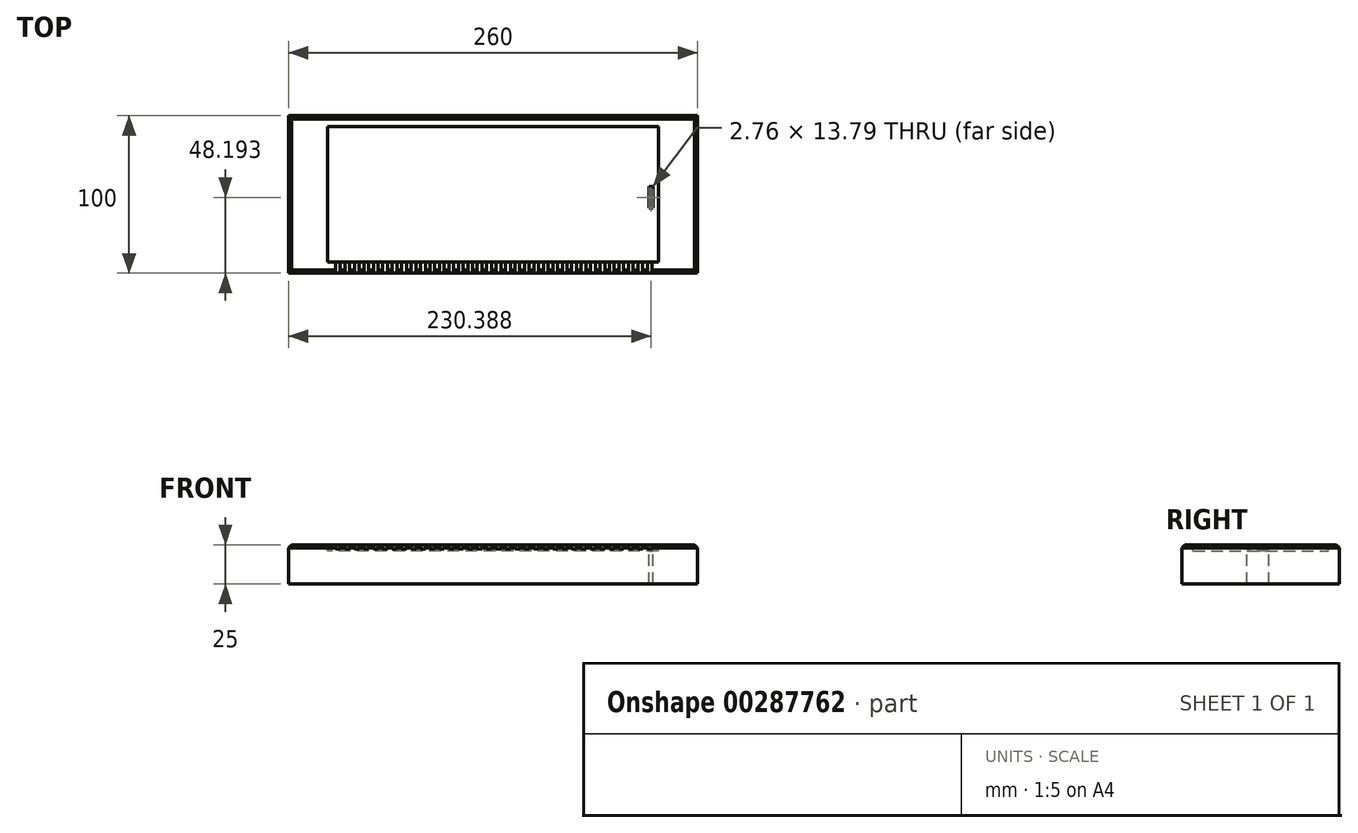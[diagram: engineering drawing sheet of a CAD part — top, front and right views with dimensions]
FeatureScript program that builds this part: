
annotation { "Feature Type Name" : "Feature", "Feature Type Description" : "" }
export const myFeature = defineFeature(function(context is Context, id is Id, definition is map)
    precondition{}
    {
        {
            var Q0;
            Q0=qCreatedBy(makeId("Top.planeOp"),FACE);
            var sketch = newSketch(context, id + "F0", { "sketchPlane" : qUnion([Q0])});
            skLineSegment(sketch, "E0.bottom", {"start": v(130, -50) * mm, "end": v(-130, -50) * mm});
            skLineSegment(sketch, "E0.top", {"start": v(130, 50) * mm, "end": v(-130, 50) * mm});
            skLineSegment(sketch, "E0.left", {"start": v(130, -50) * mm, "end": v(130, 50) * mm});
            skLineSegment(sketch, "E0.right", {"start": v(-130, -50) * mm, "end": v(-130, 50) * mm});
            skPoint(sketch, "E0.middle", {"position": v(0, 0) * mm});
            skSolve(sketch);
        }
        {
            var Q0;
            Q0 = qSketchRegion(id + "F0", true);
            extrude(context, id + "F1", {"entities" : qUnion([Q0]), "depth" : 25 * mm});
        }
        {
            var Q0;
            Q0=makeQuery(id+"F1.opExtrude","CAP_FACE",FACE,{"disambiguationData":[OSD([sQuery(id+"F0.wireOp",EDGE,"E0.bottom"),sQuery(id+"F0.wireOp",EDGE,"E0.top"),sQuery(id+"F0.wireOp",EDGE,"E0.left"),sQuery(id+"F0.wireOp",EDGE,"E0.right")])],"isStart":false});
            var sketch = newSketch(context, id + "F2", { "sketchPlane" : qUnion([Q0])});
            skLineSegment(sketch, "E1.bottom", {"start": v(105, -43) * mm, "end": v(-105, -43) * mm});
            skLineSegment(sketch, "E1.top", {"start": v(105, 43) * mm, "end": v(-105, 43) * mm});
            skLineSegment(sketch, "E1.left", {"start": v(105, -43) * mm, "end": v(105, 43) * mm});
            skLineSegment(sketch, "E1.right", {"start": v(-105, -43) * mm, "end": v(-105, 43) * mm});
            skPoint(sketch, "E1.middle", {"position": v(0, 0) * mm});
            skSolve(sketch);
        }
        {
            var Q0;
            Q0 = qSketchRegion(id + "F2", true);
            extrude(context, id + "F3", {"entities" : qUnion([Q0]), "operationType" : NewBodyOperationType.REMOVE, "oppositeDirection" : true, "depth" : 4 * mm});
        }
        {
            var Q0;
            Q0=makeQuery(id+"F1.opExtrude","CAP_FACE",FACE,{"disambiguationData":[OSD([sQuery(id+"F0.wireOp",EDGE,"E0.bottom"),sQuery(id+"F0.wireOp",EDGE,"E0.top"),sQuery(id+"F0.wireOp",EDGE,"E0.left"),sQuery(id+"F0.wireOp",EDGE,"E0.right")])],"isStart":false});
            var sketch = newSketch(context, id + "F4", { "sketchPlane" : qUnion([Q0])});
            skLineSegment(sketch, "E2.bottom", {"start": v(-100, -43) * mm, "end": v(-97, -43) * mm});
            skLineSegment(sketch, "E2.top", {"start": v(-100, -58) * mm, "end": v(-97, -58) * mm});
            skLineSegment(sketch, "E2.left", {"start": v(-100, -43) * mm, "end": v(-100, -58) * mm});
            skLineSegment(sketch, "E2.right", {"start": v(-97, -43) * mm, "end": v(-97, -58) * mm});
            skLineSegment(sketch, "E3.1.0.0", {"start": v(-94, -58) * mm, "end": v(-91, -58) * mm});
            skLineSegment(sketch, "E3.1.0.1", {"start": v(-91, -43) * mm, "end": v(-91, -58) * mm});
            skLineSegment(sketch, "E3.1.0.2", {"start": v(-94, -43) * mm, "end": v(-91, -43) * mm});
            skLineSegment(sketch, "E3.1.0.3", {"start": v(-94, -43) * mm, "end": v(-94, -58) * mm});
            skLineSegment(sketch, "E3.2.0.0", {"start": v(-88, -58) * mm, "end": v(-85, -58) * mm});
            skLineSegment(sketch, "E3.2.0.1", {"start": v(-85, -43) * mm, "end": v(-85, -58) * mm});
            skLineSegment(sketch, "E3.2.0.2", {"start": v(-88, -43) * mm, "end": v(-85, -43) * mm});
            skLineSegment(sketch, "E3.2.0.3", {"start": v(-88, -43) * mm, "end": v(-88, -58) * mm});
            skLineSegment(sketch, "E3.3.0.0", {"start": v(-82, -58) * mm, "end": v(-79, -58) * mm});
            skLineSegment(sketch, "E3.3.0.1", {"start": v(-79, -43) * mm, "end": v(-79, -58) * mm});
            skLineSegment(sketch, "E3.3.0.2", {"start": v(-82, -43) * mm, "end": v(-79, -43) * mm});
            skLineSegment(sketch, "E3.3.0.3", {"start": v(-82, -43) * mm, "end": v(-82, -58) * mm});
            skLineSegment(sketch, "E3.4.0.0", {"start": v(-76, -58) * mm, "end": v(-73, -58) * mm});
            skLineSegment(sketch, "E3.4.0.1", {"start": v(-73, -43) * mm, "end": v(-73, -58) * mm});
            skLineSegment(sketch, "E3.4.0.2", {"start": v(-76, -43) * mm, "end": v(-73, -43) * mm});
            skLineSegment(sketch, "E3.4.0.3", {"start": v(-76, -43) * mm, "end": v(-76, -58) * mm});
            skLineSegment(sketch, "E3.5.0.0", {"start": v(-70, -58) * mm, "end": v(-67, -58) * mm});
            skLineSegment(sketch, "E3.5.0.1", {"start": v(-67, -43) * mm, "end": v(-67, -58) * mm});
            skLineSegment(sketch, "E3.5.0.2", {"start": v(-70, -43) * mm, "end": v(-67, -43) * mm});
            skLineSegment(sketch, "E3.5.0.3", {"start": v(-70, -43) * mm, "end": v(-70, -58) * mm});
            skLineSegment(sketch, "E3.6.0.0", {"start": v(-64, -58) * mm, "end": v(-61, -58) * mm});
            skLineSegment(sketch, "E3.6.0.1", {"start": v(-61, -43) * mm, "end": v(-61, -58) * mm});
            skLineSegment(sketch, "E3.6.0.2", {"start": v(-64, -43) * mm, "end": v(-61, -43) * mm});
            skLineSegment(sketch, "E3.6.0.3", {"start": v(-64, -43) * mm, "end": v(-64, -58) * mm});
            skLineSegment(sketch, "E3.7.0.0", {"start": v(-58, -58) * mm, "end": v(-55, -58) * mm});
            skLineSegment(sketch, "E3.7.0.1", {"start": v(-55, -43) * mm, "end": v(-55, -58) * mm});
            skLineSegment(sketch, "E3.7.0.2", {"start": v(-58, -43) * mm, "end": v(-55, -43) * mm});
            skLineSegment(sketch, "E3.7.0.3", {"start": v(-58, -43) * mm, "end": v(-58, -58) * mm});
            skLineSegment(sketch, "E3.8.0.0", {"start": v(-52, -58) * mm, "end": v(-49, -58) * mm});
            skLineSegment(sketch, "E3.8.0.1", {"start": v(-49, -43) * mm, "end": v(-49, -58) * mm});
            skLineSegment(sketch, "E3.8.0.2", {"start": v(-52, -43) * mm, "end": v(-49, -43) * mm});
            skLineSegment(sketch, "E3.8.0.3", {"start": v(-52, -43) * mm, "end": v(-52, -58) * mm});
            skLineSegment(sketch, "E3.9.0.0", {"start": v(-46, -58) * mm, "end": v(-43, -58) * mm});
            skLineSegment(sketch, "E3.9.0.1", {"start": v(-43, -43) * mm, "end": v(-43, -58) * mm});
            skLineSegment(sketch, "E3.9.0.2", {"start": v(-46, -43) * mm, "end": v(-43, -43) * mm});
            skLineSegment(sketch, "E3.9.0.3", {"start": v(-46, -43) * mm, "end": v(-46, -58) * mm});
            skLineSegment(sketch, "E3.10.0.0", {"start": v(-40, -58) * mm, "end": v(-37, -58) * mm});
            skLineSegment(sketch, "E3.10.0.1", {"start": v(-37, -43) * mm, "end": v(-37, -58) * mm});
            skLineSegment(sketch, "E3.10.0.2", {"start": v(-40, -43) * mm, "end": v(-37, -43) * mm});
            skLineSegment(sketch, "E3.10.0.3", {"start": v(-40, -43) * mm, "end": v(-40, -58) * mm});
            skLineSegment(sketch, "E3.11.0.0", {"start": v(-34, -58) * mm, "end": v(-31, -58) * mm});
            skLineSegment(sketch, "E3.11.0.1", {"start": v(-31, -43) * mm, "end": v(-31, -58) * mm});
            skLineSegment(sketch, "E3.11.0.2", {"start": v(-34, -43) * mm, "end": v(-31, -43) * mm});
            skLineSegment(sketch, "E3.11.0.3", {"start": v(-34, -43) * mm, "end": v(-34, -58) * mm});
            skLineSegment(sketch, "E3.12.0.0", {"start": v(-28, -58) * mm, "end": v(-25, -58) * mm});
            skLineSegment(sketch, "E3.12.0.1", {"start": v(-25, -43) * mm, "end": v(-25, -58) * mm});
            skLineSegment(sketch, "E3.12.0.2", {"start": v(-28, -43) * mm, "end": v(-25, -43) * mm});
            skLineSegment(sketch, "E3.12.0.3", {"start": v(-28, -43) * mm, "end": v(-28, -58) * mm});
            skLineSegment(sketch, "E3.13.0.0", {"start": v(-22, -58) * mm, "end": v(-19, -58) * mm});
            skLineSegment(sketch, "E3.13.0.1", {"start": v(-19, -43) * mm, "end": v(-19, -58) * mm});
            skLineSegment(sketch, "E3.13.0.2", {"start": v(-22, -43) * mm, "end": v(-19, -43) * mm});
            skLineSegment(sketch, "E3.13.0.3", {"start": v(-22, -43) * mm, "end": v(-22, -58) * mm});
            skLineSegment(sketch, "E3.14.0.0", {"start": v(-16, -58) * mm, "end": v(-13, -58) * mm});
            skLineSegment(sketch, "E3.14.0.1", {"start": v(-13, -43) * mm, "end": v(-13, -58) * mm});
            skLineSegment(sketch, "E3.14.0.2", {"start": v(-16, -43) * mm, "end": v(-13, -43) * mm});
            skLineSegment(sketch, "E3.14.0.3", {"start": v(-16, -43) * mm, "end": v(-16, -58) * mm});
            skLineSegment(sketch, "E3.15.0.0", {"start": v(-10, -58) * mm, "end": v(-7, -58) * mm});
            skLineSegment(sketch, "E3.15.0.1", {"start": v(-7, -43) * mm, "end": v(-7, -58) * mm});
            skLineSegment(sketch, "E3.15.0.2", {"start": v(-10, -43) * mm, "end": v(-7, -43) * mm});
            skLineSegment(sketch, "E3.15.0.3", {"start": v(-10, -43) * mm, "end": v(-10, -58) * mm});
            skLineSegment(sketch, "E3.16.0.0", {"start": v(-4, -58) * mm, "end": v(-1, -58) * mm});
            skLineSegment(sketch, "E3.16.0.1", {"start": v(-1, -43) * mm, "end": v(-1, -58) * mm});
            skLineSegment(sketch, "E3.16.0.2", {"start": v(-4, -43) * mm, "end": v(-1, -43) * mm});
            skLineSegment(sketch, "E3.16.0.3", {"start": v(-4, -43) * mm, "end": v(-4, -58) * mm});
            skLineSegment(sketch, "E3.17.0.0", {"start": v(2, -58) * mm, "end": v(5, -58) * mm});
            skLineSegment(sketch, "E3.17.0.1", {"start": v(5, -43) * mm, "end": v(5, -58) * mm});
            skLineSegment(sketch, "E3.17.0.2", {"start": v(2, -43) * mm, "end": v(5, -43) * mm});
            skLineSegment(sketch, "E3.17.0.3", {"start": v(2, -43) * mm, "end": v(2, -58) * mm});
            skLineSegment(sketch, "E3.18.0.0", {"start": v(8, -58) * mm, "end": v(11, -58) * mm});
            skLineSegment(sketch, "E3.18.0.1", {"start": v(11, -43) * mm, "end": v(11, -58) * mm});
            skLineSegment(sketch, "E3.18.0.2", {"start": v(8, -43) * mm, "end": v(11, -43) * mm});
            skLineSegment(sketch, "E3.18.0.3", {"start": v(8, -43) * mm, "end": v(8, -58) * mm});
            skLineSegment(sketch, "E3.19.0.0", {"start": v(14, -58) * mm, "end": v(17, -58) * mm});
            skLineSegment(sketch, "E3.19.0.1", {"start": v(17, -43) * mm, "end": v(17, -58) * mm});
            skLineSegment(sketch, "E3.19.0.2", {"start": v(14, -43) * mm, "end": v(17, -43) * mm});
            skLineSegment(sketch, "E3.19.0.3", {"start": v(14, -43) * mm, "end": v(14, -58) * mm});
            skLineSegment(sketch, "E3.20.0.0", {"start": v(20, -58) * mm, "end": v(23, -58) * mm});
            skLineSegment(sketch, "E3.20.0.1", {"start": v(23, -43) * mm, "end": v(23, -58) * mm});
            skLineSegment(sketch, "E3.20.0.2", {"start": v(20, -43) * mm, "end": v(23, -43) * mm});
            skLineSegment(sketch, "E3.20.0.3", {"start": v(20, -43) * mm, "end": v(20, -58) * mm});
            skLineSegment(sketch, "E3.21.0.0", {"start": v(26, -58) * mm, "end": v(29, -58) * mm});
            skLineSegment(sketch, "E3.21.0.1", {"start": v(29, -43) * mm, "end": v(29, -58) * mm});
            skLineSegment(sketch, "E3.21.0.2", {"start": v(26, -43) * mm, "end": v(29, -43) * mm});
            skLineSegment(sketch, "E3.21.0.3", {"start": v(26, -43) * mm, "end": v(26, -58) * mm});
            skLineSegment(sketch, "E3.22.0.0", {"start": v(32, -58) * mm, "end": v(35, -58) * mm});
            skLineSegment(sketch, "E3.22.0.1", {"start": v(35, -43) * mm, "end": v(35, -58) * mm});
            skLineSegment(sketch, "E3.22.0.2", {"start": v(32, -43) * mm, "end": v(35, -43) * mm});
            skLineSegment(sketch, "E3.22.0.3", {"start": v(32, -43) * mm, "end": v(32, -58) * mm});
            skLineSegment(sketch, "E3.23.0.0", {"start": v(38, -58) * mm, "end": v(41, -58) * mm});
            skLineSegment(sketch, "E3.23.0.1", {"start": v(41, -43) * mm, "end": v(41, -58) * mm});
            skLineSegment(sketch, "E3.23.0.2", {"start": v(38, -43) * mm, "end": v(41, -43) * mm});
            skLineSegment(sketch, "E3.23.0.3", {"start": v(38, -43) * mm, "end": v(38, -58) * mm});
            skLineSegment(sketch, "E3.24.0.0", {"start": v(44, -58) * mm, "end": v(47, -58) * mm});
            skLineSegment(sketch, "E3.24.0.1", {"start": v(47, -43) * mm, "end": v(47, -58) * mm});
            skLineSegment(sketch, "E3.24.0.2", {"start": v(44, -43) * mm, "end": v(47, -43) * mm});
            skLineSegment(sketch, "E3.24.0.3", {"start": v(44, -43) * mm, "end": v(44, -58) * mm});
            skLineSegment(sketch, "E3.25.0.0", {"start": v(50, -58) * mm, "end": v(53, -58) * mm});
            skLineSegment(sketch, "E3.25.0.1", {"start": v(53, -43) * mm, "end": v(53, -58) * mm});
            skLineSegment(sketch, "E3.25.0.2", {"start": v(50, -43) * mm, "end": v(53, -43) * mm});
            skLineSegment(sketch, "E3.25.0.3", {"start": v(50, -43) * mm, "end": v(50, -58) * mm});
            skLineSegment(sketch, "E3.26.0.0", {"start": v(56, -58) * mm, "end": v(59, -58) * mm});
            skLineSegment(sketch, "E3.26.0.1", {"start": v(59, -43) * mm, "end": v(59, -58) * mm});
            skLineSegment(sketch, "E3.26.0.2", {"start": v(56, -43) * mm, "end": v(59, -43) * mm});
            skLineSegment(sketch, "E3.26.0.3", {"start": v(56, -43) * mm, "end": v(56, -58) * mm});
            skLineSegment(sketch, "E3.27.0.0", {"start": v(62, -58) * mm, "end": v(65, -58) * mm});
            skLineSegment(sketch, "E3.27.0.1", {"start": v(65, -43) * mm, "end": v(65, -58) * mm});
            skLineSegment(sketch, "E3.27.0.2", {"start": v(62, -43) * mm, "end": v(65, -43) * mm});
            skLineSegment(sketch, "E3.27.0.3", {"start": v(62, -43) * mm, "end": v(62, -58) * mm});
            skLineSegment(sketch, "E3.28.0.0", {"start": v(68, -58) * mm, "end": v(71, -58) * mm});
            skLineSegment(sketch, "E3.28.0.1", {"start": v(71, -43) * mm, "end": v(71, -58) * mm});
            skLineSegment(sketch, "E3.28.0.2", {"start": v(68, -43) * mm, "end": v(71, -43) * mm});
            skLineSegment(sketch, "E3.28.0.3", {"start": v(68, -43) * mm, "end": v(68, -58) * mm});
            skLineSegment(sketch, "E3.29.0.0", {"start": v(74, -58) * mm, "end": v(77, -58) * mm});
            skLineSegment(sketch, "E3.29.0.1", {"start": v(77, -43) * mm, "end": v(77, -58) * mm});
            skLineSegment(sketch, "E3.29.0.2", {"start": v(74, -43) * mm, "end": v(77, -43) * mm});
            skLineSegment(sketch, "E3.29.0.3", {"start": v(74, -43) * mm, "end": v(74, -58) * mm});
            skLineSegment(sketch, "E3.30.0.0", {"start": v(80, -58) * mm, "end": v(83, -58) * mm});
            skLineSegment(sketch, "E3.30.0.1", {"start": v(83, -43) * mm, "end": v(83, -58) * mm});
            skLineSegment(sketch, "E3.30.0.2", {"start": v(80, -43) * mm, "end": v(83, -43) * mm});
            skLineSegment(sketch, "E3.30.0.3", {"start": v(80, -43) * mm, "end": v(80, -58) * mm});
            skLineSegment(sketch, "E3.31.0.0", {"start": v(86, -58) * mm, "end": v(89, -58) * mm});
            skLineSegment(sketch, "E3.31.0.1", {"start": v(89, -43) * mm, "end": v(89, -58) * mm});
            skLineSegment(sketch, "E3.31.0.2", {"start": v(86, -43) * mm, "end": v(89, -43) * mm});
            skLineSegment(sketch, "E3.31.0.3", {"start": v(86, -43) * mm, "end": v(86, -58) * mm});
            skLineSegment(sketch, "E3.32.0.0", {"start": v(92, -58) * mm, "end": v(95, -58) * mm});
            skLineSegment(sketch, "E3.32.0.1", {"start": v(95, -43) * mm, "end": v(95, -58) * mm});
            skLineSegment(sketch, "E3.32.0.2", {"start": v(92, -43) * mm, "end": v(95, -43) * mm});
            skLineSegment(sketch, "E3.32.0.3", {"start": v(92, -43) * mm, "end": v(92, -58) * mm});
            skLineSegment(sketch, "E3.33.0.0", {"start": v(98, -58) * mm, "end": v(101, -58) * mm});
            skLineSegment(sketch, "E3.33.0.1", {"start": v(101, -43) * mm, "end": v(101, -58) * mm});
            skLineSegment(sketch, "E3.33.0.2", {"start": v(98, -43) * mm, "end": v(101, -43) * mm});
            skLineSegment(sketch, "E3.33.0.3", {"start": v(98, -43) * mm, "end": v(98, -58) * mm});
            skLineSegment(sketch, "E3.direction1", {"start": v(-100, -58) * mm, "end": v(-94, -58) * mm, "construction": true});
            skSolve(sketch);
        }
        {
            var Q0;
            Q0 = qSketchRegion(id + "F4", true);
            extrude(context, id + "F5", {"entities" : qUnion([Q0]), "operationType" : NewBodyOperationType.REMOVE, "oppositeDirection" : true, "depth" : 2.5 * mm});
        }
        {
            var Q0;
            Q0=makeQuery(id+"F3.boolean.opBoolean","COPY",FACE,{"derivedFrom":makeQuery(id+"F3.opExtrude","CAP_FACE",FACE,{"disambiguationData":[OSD([sQuery(id+"F2.wireOp",EDGE,"E1.bottom"),sQuery(id+"F2.wireOp",EDGE,"E1.top"),sQuery(id+"F2.wireOp",EDGE,"E1.left"),sQuery(id+"F2.wireOp",EDGE,"E1.right")])],"isStart":false})});
            var sketch = newSketch(context, id + "F6", { "sketchPlane" : qUnion([Q0])});
            skLineSegment(sketch, "E4.bottom", {"start": v(105, -43) * mm, "end": v(96.17, -43) * mm, "construction": true});
            skLineSegment(sketch, "E4.top", {"start": v(105, 43) * mm, "end": v(96.17, 43) * mm, "construction": true});
            skLineSegment(sketch, "E4.left", {"start": v(105, -43) * mm, "end": v(105, 43) * mm, "construction": true});
            skLineSegment(sketch, "E4.right", {"start": v(96.17, -43) * mm, "end": v(96.17, 43) * mm, "construction": true});
            skLineSegment(sketch, "E5.bottom", {"start": v(99, 5.1) * mm, "end": v(101.77, 5.1) * mm});
            skLineSegment(sketch, "E5.top", {"start": v(99, -8.7) * mm, "end": v(101.77, -8.7) * mm});
            skLineSegment(sketch, "E5.left", {"start": v(99, 5.1) * mm, "end": v(99, -8.7) * mm});
            skLineSegment(sketch, "E5.right", {"start": v(101.77, 5.1) * mm, "end": v(101.77, -8.7) * mm});
            skSolve(sketch);
        }
        {
            var Q0;
            Q0=makeQuery(id+"F1.opExtrude","CAP_EDGE",EDGE,{"disambiguationData":[OSD([sQuery(id+"F0.wireOp",EDGE,"E0.left")])],"isStart":false});
            var Q1;
            Q1=makeQuery(id+"F1.opExtrude","CAP_EDGE",EDGE,{"disambiguationData":[OSD([sQuery(id+"F0.wireOp",EDGE,"E0.top")])],"isStart":false});
            var Q2;
            {var subQ0=sQuery(id+"F0.wireOp",EDGE,"E0.bottom");var subQ1=sQuery(id+"F0.wireOp",EDGE,"E0.left");Q2=makeQuery(id+"F5.boolean.opBoolean","SPLIT",EDGE,{"disambiguationData":[TD([makeQuery(id+"F1.opExtrude","SWEPT_FACE",FACE,{"disambiguationData":[OSD([subQ1])]})])],"derivedFrom":makeQuery(id+"F1.opExtrude","CAP_EDGE",EDGE,{"disambiguationData":[OSD([subQ0])],"isStart":false})});}
            var Q3;
            Q3=makeQuery(id+"F1.opExtrude","CAP_EDGE",EDGE,{"disambiguationData":[OSD([sQuery(id+"F0.wireOp",EDGE,"E0.right")])],"isStart":false});
            chamfer(context, id + "F7", {"entities" : qUnion([Q0, Q1, Q2, Q3]), "width" : 2 * mm, "tangentPropagation" : true});
        }
        {
            var Q0;
            {var subQ0=sQuery(id+"F0.wireOp",EDGE,"E0.bottom");var subQ1=sQuery(id+"F0.wireOp",EDGE,"E0.right");Q0=makeQuery(id+"F5.boolean.opBoolean","SPLIT",EDGE,{"disambiguationData":[TD([makeQuery(id+"F1.opExtrude","SWEPT_FACE",FACE,{"disambiguationData":[OSD([subQ1])]})])],"derivedFrom":makeQuery(id+"F1.opExtrude","CAP_EDGE",EDGE,{"disambiguationData":[OSD([subQ0])],"isStart":false})});}
            var Q1;
            {var subQ0=sQuery(id+"F0.wireOp",EDGE,"E0.bottom");Q1=makeQuery(id+"F5.boolean.opBoolean","SPLIT",EDGE,{"disambiguationData":[TD([makeQuery(id+"F5.opExtrude","SWEPT_FACE",FACE,{"disambiguationData":[OSD([sQuery(id+"F4.wireOp",EDGE,"E2.right")])]})])],"derivedFrom":makeQuery(id+"F1.opExtrude","CAP_EDGE",EDGE,{"disambiguationData":[OSD([subQ0])],"isStart":false})});}
            var Q2;
            {var subQ0=sQuery(id+"F0.wireOp",EDGE,"E0.bottom");Q2=makeQuery(id+"F5.boolean.opBoolean","SPLIT",EDGE,{"disambiguationData":[TD([makeQuery(id+"F5.opExtrude","SWEPT_FACE",FACE,{"disambiguationData":[OSD([sQuery(id+"F4.wireOp",EDGE,"E3.1.0.1")])]})])],"derivedFrom":makeQuery(id+"F1.opExtrude","CAP_EDGE",EDGE,{"disambiguationData":[OSD([subQ0])],"isStart":false})});}
            var Q3;
            {var subQ0=sQuery(id+"F0.wireOp",EDGE,"E0.bottom");Q3=makeQuery(id+"F5.boolean.opBoolean","SPLIT",EDGE,{"disambiguationData":[TD([makeQuery(id+"F5.opExtrude","SWEPT_FACE",FACE,{"disambiguationData":[OSD([sQuery(id+"F4.wireOp",EDGE,"E3.2.0.1")])]})])],"derivedFrom":makeQuery(id+"F1.opExtrude","CAP_EDGE",EDGE,{"disambiguationData":[OSD([subQ0])],"isStart":false})});}
            var Q4;
            {var subQ0=sQuery(id+"F0.wireOp",EDGE,"E0.bottom");Q4=makeQuery(id+"F5.boolean.opBoolean","SPLIT",EDGE,{"disambiguationData":[TD([makeQuery(id+"F5.opExtrude","SWEPT_FACE",FACE,{"disambiguationData":[OSD([sQuery(id+"F4.wireOp",EDGE,"E3.3.0.1")])]})])],"derivedFrom":makeQuery(id+"F1.opExtrude","CAP_EDGE",EDGE,{"disambiguationData":[OSD([subQ0])],"isStart":false})});}
            var Q5;
            {var subQ0=sQuery(id+"F0.wireOp",EDGE,"E0.bottom");Q5=makeQuery(id+"F5.boolean.opBoolean","SPLIT",EDGE,{"disambiguationData":[TD([makeQuery(id+"F5.opExtrude","SWEPT_FACE",FACE,{"disambiguationData":[OSD([sQuery(id+"F4.wireOp",EDGE,"E3.4.0.1")])]})])],"derivedFrom":makeQuery(id+"F1.opExtrude","CAP_EDGE",EDGE,{"disambiguationData":[OSD([subQ0])],"isStart":false})});}
            var Q6;
            {var subQ0=sQuery(id+"F0.wireOp",EDGE,"E0.bottom");Q6=makeQuery(id+"F5.boolean.opBoolean","SPLIT",EDGE,{"disambiguationData":[TD([makeQuery(id+"F5.opExtrude","SWEPT_FACE",FACE,{"disambiguationData":[OSD([sQuery(id+"F4.wireOp",EDGE,"E3.5.0.1")])]})])],"derivedFrom":makeQuery(id+"F1.opExtrude","CAP_EDGE",EDGE,{"disambiguationData":[OSD([subQ0])],"isStart":false})});}
            var Q7;
            {var subQ0=sQuery(id+"F0.wireOp",EDGE,"E0.bottom");Q7=makeQuery(id+"F5.boolean.opBoolean","SPLIT",EDGE,{"disambiguationData":[TD([makeQuery(id+"F5.opExtrude","SWEPT_FACE",FACE,{"disambiguationData":[OSD([sQuery(id+"F4.wireOp",EDGE,"E3.6.0.1")])]})])],"derivedFrom":makeQuery(id+"F1.opExtrude","CAP_EDGE",EDGE,{"disambiguationData":[OSD([subQ0])],"isStart":false})});}
            var Q8;
            {var subQ0=sQuery(id+"F0.wireOp",EDGE,"E0.bottom");Q8=makeQuery(id+"F5.boolean.opBoolean","SPLIT",EDGE,{"disambiguationData":[TD([makeQuery(id+"F5.opExtrude","SWEPT_FACE",FACE,{"disambiguationData":[OSD([sQuery(id+"F4.wireOp",EDGE,"E3.7.0.1")])]})])],"derivedFrom":makeQuery(id+"F1.opExtrude","CAP_EDGE",EDGE,{"disambiguationData":[OSD([subQ0])],"isStart":false})});}
            var Q9;
            {var subQ0=sQuery(id+"F0.wireOp",EDGE,"E0.bottom");Q9=makeQuery(id+"F5.boolean.opBoolean","SPLIT",EDGE,{"disambiguationData":[TD([makeQuery(id+"F5.opExtrude","SWEPT_FACE",FACE,{"disambiguationData":[OSD([sQuery(id+"F4.wireOp",EDGE,"E3.8.0.1")])]})])],"derivedFrom":makeQuery(id+"F1.opExtrude","CAP_EDGE",EDGE,{"disambiguationData":[OSD([subQ0])],"isStart":false})});}
            var Q10;
            {var subQ0=sQuery(id+"F0.wireOp",EDGE,"E0.bottom");Q10=makeQuery(id+"F5.boolean.opBoolean","SPLIT",EDGE,{"disambiguationData":[TD([makeQuery(id+"F5.opExtrude","SWEPT_FACE",FACE,{"disambiguationData":[OSD([sQuery(id+"F4.wireOp",EDGE,"E3.9.0.1")])]})])],"derivedFrom":makeQuery(id+"F1.opExtrude","CAP_EDGE",EDGE,{"disambiguationData":[OSD([subQ0])],"isStart":false})});}
            var Q11;
            {var subQ0=sQuery(id+"F0.wireOp",EDGE,"E0.bottom");Q11=makeQuery(id+"F5.boolean.opBoolean","SPLIT",EDGE,{"disambiguationData":[TD([makeQuery(id+"F5.opExtrude","SWEPT_FACE",FACE,{"disambiguationData":[OSD([sQuery(id+"F4.wireOp",EDGE,"E3.10.0.1")])]})])],"derivedFrom":makeQuery(id+"F1.opExtrude","CAP_EDGE",EDGE,{"disambiguationData":[OSD([subQ0])],"isStart":false})});}
            var Q12;
            {var subQ0=sQuery(id+"F0.wireOp",EDGE,"E0.bottom");Q12=makeQuery(id+"F5.boolean.opBoolean","SPLIT",EDGE,{"disambiguationData":[TD([makeQuery(id+"F5.opExtrude","SWEPT_FACE",FACE,{"disambiguationData":[OSD([sQuery(id+"F4.wireOp",EDGE,"E3.11.0.1")])]})])],"derivedFrom":makeQuery(id+"F1.opExtrude","CAP_EDGE",EDGE,{"disambiguationData":[OSD([subQ0])],"isStart":false})});}
            var Q13;
            {var subQ0=sQuery(id+"F0.wireOp",EDGE,"E0.bottom");Q13=makeQuery(id+"F5.boolean.opBoolean","SPLIT",EDGE,{"disambiguationData":[TD([makeQuery(id+"F5.opExtrude","SWEPT_FACE",FACE,{"disambiguationData":[OSD([sQuery(id+"F4.wireOp",EDGE,"E3.12.0.1")])]})])],"derivedFrom":makeQuery(id+"F1.opExtrude","CAP_EDGE",EDGE,{"disambiguationData":[OSD([subQ0])],"isStart":false})});}
            var Q14;
            {var subQ0=sQuery(id+"F0.wireOp",EDGE,"E0.bottom");Q14=makeQuery(id+"F5.boolean.opBoolean","SPLIT",EDGE,{"disambiguationData":[TD([makeQuery(id+"F5.opExtrude","SWEPT_FACE",FACE,{"disambiguationData":[OSD([sQuery(id+"F4.wireOp",EDGE,"E3.13.0.1")])]})])],"derivedFrom":makeQuery(id+"F1.opExtrude","CAP_EDGE",EDGE,{"disambiguationData":[OSD([subQ0])],"isStart":false})});}
            var Q15;
            {var subQ0=sQuery(id+"F0.wireOp",EDGE,"E0.bottom");Q15=makeQuery(id+"F5.boolean.opBoolean","SPLIT",EDGE,{"disambiguationData":[TD([makeQuery(id+"F5.opExtrude","SWEPT_FACE",FACE,{"disambiguationData":[OSD([sQuery(id+"F4.wireOp",EDGE,"E3.14.0.1")])]})])],"derivedFrom":makeQuery(id+"F1.opExtrude","CAP_EDGE",EDGE,{"disambiguationData":[OSD([subQ0])],"isStart":false})});}
            var Q16;
            {var subQ0=sQuery(id+"F0.wireOp",EDGE,"E0.bottom");Q16=makeQuery(id+"F5.boolean.opBoolean","SPLIT",EDGE,{"disambiguationData":[TD([makeQuery(id+"F5.opExtrude","SWEPT_FACE",FACE,{"disambiguationData":[OSD([sQuery(id+"F4.wireOp",EDGE,"E3.15.0.1")])]})])],"derivedFrom":makeQuery(id+"F1.opExtrude","CAP_EDGE",EDGE,{"disambiguationData":[OSD([subQ0])],"isStart":false})});}
            var Q17;
            {var subQ0=sQuery(id+"F0.wireOp",EDGE,"E0.bottom");Q17=makeQuery(id+"F5.boolean.opBoolean","SPLIT",EDGE,{"disambiguationData":[TD([makeQuery(id+"F5.opExtrude","SWEPT_FACE",FACE,{"disambiguationData":[OSD([sQuery(id+"F4.wireOp",EDGE,"E3.16.0.1")])]})])],"derivedFrom":makeQuery(id+"F1.opExtrude","CAP_EDGE",EDGE,{"disambiguationData":[OSD([subQ0])],"isStart":false})});}
            var Q18;
            {var subQ0=sQuery(id+"F0.wireOp",EDGE,"E0.bottom");Q18=makeQuery(id+"F5.boolean.opBoolean","SPLIT",EDGE,{"disambiguationData":[TD([makeQuery(id+"F5.opExtrude","SWEPT_FACE",FACE,{"disambiguationData":[OSD([sQuery(id+"F4.wireOp",EDGE,"E3.17.0.1")])]})])],"derivedFrom":makeQuery(id+"F1.opExtrude","CAP_EDGE",EDGE,{"disambiguationData":[OSD([subQ0])],"isStart":false})});}
            var Q19;
            {var subQ0=sQuery(id+"F0.wireOp",EDGE,"E0.bottom");Q19=makeQuery(id+"F5.boolean.opBoolean","SPLIT",EDGE,{"disambiguationData":[TD([makeQuery(id+"F5.opExtrude","SWEPT_FACE",FACE,{"disambiguationData":[OSD([sQuery(id+"F4.wireOp",EDGE,"E3.18.0.1")])]})])],"derivedFrom":makeQuery(id+"F1.opExtrude","CAP_EDGE",EDGE,{"disambiguationData":[OSD([subQ0])],"isStart":false})});}
            var Q20;
            {var subQ0=sQuery(id+"F0.wireOp",EDGE,"E0.bottom");Q20=makeQuery(id+"F5.boolean.opBoolean","SPLIT",EDGE,{"disambiguationData":[TD([makeQuery(id+"F5.opExtrude","SWEPT_FACE",FACE,{"disambiguationData":[OSD([sQuery(id+"F4.wireOp",EDGE,"E3.19.0.1")])]})])],"derivedFrom":makeQuery(id+"F1.opExtrude","CAP_EDGE",EDGE,{"disambiguationData":[OSD([subQ0])],"isStart":false})});}
            var Q21;
            {var subQ0=sQuery(id+"F0.wireOp",EDGE,"E0.bottom");Q21=makeQuery(id+"F5.boolean.opBoolean","SPLIT",EDGE,{"disambiguationData":[TD([makeQuery(id+"F5.opExtrude","SWEPT_FACE",FACE,{"disambiguationData":[OSD([sQuery(id+"F4.wireOp",EDGE,"E3.20.0.1")])]})])],"derivedFrom":makeQuery(id+"F1.opExtrude","CAP_EDGE",EDGE,{"disambiguationData":[OSD([subQ0])],"isStart":false})});}
            var Q22;
            {var subQ0=sQuery(id+"F0.wireOp",EDGE,"E0.bottom");Q22=makeQuery(id+"F5.boolean.opBoolean","SPLIT",EDGE,{"disambiguationData":[TD([makeQuery(id+"F5.opExtrude","SWEPT_FACE",FACE,{"disambiguationData":[OSD([sQuery(id+"F4.wireOp",EDGE,"E3.21.0.1")])]})])],"derivedFrom":makeQuery(id+"F1.opExtrude","CAP_EDGE",EDGE,{"disambiguationData":[OSD([subQ0])],"isStart":false})});}
            var Q23;
            {var subQ0=sQuery(id+"F0.wireOp",EDGE,"E0.bottom");Q23=makeQuery(id+"F5.boolean.opBoolean","SPLIT",EDGE,{"disambiguationData":[TD([makeQuery(id+"F5.opExtrude","SWEPT_FACE",FACE,{"disambiguationData":[OSD([sQuery(id+"F4.wireOp",EDGE,"E3.22.0.1")])]})])],"derivedFrom":makeQuery(id+"F1.opExtrude","CAP_EDGE",EDGE,{"disambiguationData":[OSD([subQ0])],"isStart":false})});}
            var Q24;
            {var subQ0=sQuery(id+"F0.wireOp",EDGE,"E0.bottom");Q24=makeQuery(id+"F5.boolean.opBoolean","SPLIT",EDGE,{"disambiguationData":[TD([makeQuery(id+"F5.opExtrude","SWEPT_FACE",FACE,{"disambiguationData":[OSD([sQuery(id+"F4.wireOp",EDGE,"E3.23.0.1")])]})])],"derivedFrom":makeQuery(id+"F1.opExtrude","CAP_EDGE",EDGE,{"disambiguationData":[OSD([subQ0])],"isStart":false})});}
            var Q25;
            {var subQ0=sQuery(id+"F0.wireOp",EDGE,"E0.bottom");Q25=makeQuery(id+"F5.boolean.opBoolean","SPLIT",EDGE,{"disambiguationData":[TD([makeQuery(id+"F5.opExtrude","SWEPT_FACE",FACE,{"disambiguationData":[OSD([sQuery(id+"F4.wireOp",EDGE,"E3.24.0.1")])]})])],"derivedFrom":makeQuery(id+"F1.opExtrude","CAP_EDGE",EDGE,{"disambiguationData":[OSD([subQ0])],"isStart":false})});}
            var Q26;
            {var subQ0=sQuery(id+"F0.wireOp",EDGE,"E0.bottom");Q26=makeQuery(id+"F5.boolean.opBoolean","SPLIT",EDGE,{"disambiguationData":[TD([makeQuery(id+"F5.opExtrude","SWEPT_FACE",FACE,{"disambiguationData":[OSD([sQuery(id+"F4.wireOp",EDGE,"E3.25.0.1")])]})])],"derivedFrom":makeQuery(id+"F1.opExtrude","CAP_EDGE",EDGE,{"disambiguationData":[OSD([subQ0])],"isStart":false})});}
            var Q27;
            {var subQ0=sQuery(id+"F0.wireOp",EDGE,"E0.bottom");Q27=makeQuery(id+"F5.boolean.opBoolean","SPLIT",EDGE,{"disambiguationData":[TD([makeQuery(id+"F5.opExtrude","SWEPT_FACE",FACE,{"disambiguationData":[OSD([sQuery(id+"F4.wireOp",EDGE,"E3.26.0.1")])]})])],"derivedFrom":makeQuery(id+"F1.opExtrude","CAP_EDGE",EDGE,{"disambiguationData":[OSD([subQ0])],"isStart":false})});}
            var Q28;
            {var subQ0=sQuery(id+"F0.wireOp",EDGE,"E0.bottom");Q28=makeQuery(id+"F5.boolean.opBoolean","SPLIT",EDGE,{"disambiguationData":[TD([makeQuery(id+"F5.opExtrude","SWEPT_FACE",FACE,{"disambiguationData":[OSD([sQuery(id+"F4.wireOp",EDGE,"E3.27.0.1")])]})])],"derivedFrom":makeQuery(id+"F1.opExtrude","CAP_EDGE",EDGE,{"disambiguationData":[OSD([subQ0])],"isStart":false})});}
            var Q29;
            {var subQ0=sQuery(id+"F0.wireOp",EDGE,"E0.bottom");Q29=makeQuery(id+"F5.boolean.opBoolean","SPLIT",EDGE,{"disambiguationData":[TD([makeQuery(id+"F5.opExtrude","SWEPT_FACE",FACE,{"disambiguationData":[OSD([sQuery(id+"F4.wireOp",EDGE,"E3.28.0.1")])]})])],"derivedFrom":makeQuery(id+"F1.opExtrude","CAP_EDGE",EDGE,{"disambiguationData":[OSD([subQ0])],"isStart":false})});}
            var Q30;
            {var subQ0=sQuery(id+"F0.wireOp",EDGE,"E0.bottom");Q30=makeQuery(id+"F5.boolean.opBoolean","SPLIT",EDGE,{"disambiguationData":[TD([makeQuery(id+"F5.opExtrude","SWEPT_FACE",FACE,{"disambiguationData":[OSD([sQuery(id+"F4.wireOp",EDGE,"E3.29.0.1")])]})])],"derivedFrom":makeQuery(id+"F1.opExtrude","CAP_EDGE",EDGE,{"disambiguationData":[OSD([subQ0])],"isStart":false})});}
            var Q31;
            {var subQ0=sQuery(id+"F0.wireOp",EDGE,"E0.bottom");Q31=makeQuery(id+"F5.boolean.opBoolean","SPLIT",EDGE,{"disambiguationData":[TD([makeQuery(id+"F5.opExtrude","SWEPT_FACE",FACE,{"disambiguationData":[OSD([sQuery(id+"F4.wireOp",EDGE,"E3.30.0.1")])]})])],"derivedFrom":makeQuery(id+"F1.opExtrude","CAP_EDGE",EDGE,{"disambiguationData":[OSD([subQ0])],"isStart":false})});}
            var Q32;
            {var subQ0=sQuery(id+"F0.wireOp",EDGE,"E0.bottom");Q32=makeQuery(id+"F5.boolean.opBoolean","SPLIT",EDGE,{"disambiguationData":[TD([makeQuery(id+"F5.opExtrude","SWEPT_FACE",FACE,{"disambiguationData":[OSD([sQuery(id+"F4.wireOp",EDGE,"E3.31.0.1")])]})])],"derivedFrom":makeQuery(id+"F1.opExtrude","CAP_EDGE",EDGE,{"disambiguationData":[OSD([subQ0])],"isStart":false})});}
            var Q33;
            {var subQ0=sQuery(id+"F0.wireOp",EDGE,"E0.bottom");Q33=makeQuery(id+"F5.boolean.opBoolean","SPLIT",EDGE,{"disambiguationData":[TD([makeQuery(id+"F5.opExtrude","SWEPT_FACE",FACE,{"disambiguationData":[OSD([sQuery(id+"F4.wireOp",EDGE,"E3.32.0.1")])]})])],"derivedFrom":makeQuery(id+"F1.opExtrude","CAP_EDGE",EDGE,{"disambiguationData":[OSD([subQ0])],"isStart":false})});}
            chamfer(context, id + "F8", {"entities" : qUnion([Q0, Q1, Q2, Q3, Q4, Q5, Q6, Q7, Q8, Q9, Q10, Q11, Q12, Q13, Q14, Q15, Q16, Q17, Q18, Q19, Q20, Q21, Q22, Q23, Q24, Q25, Q26, Q27, Q28, Q29, Q30, Q31, Q32, Q33]), "width" : 2 * mm, "tangentPropagation" : true});
        }
        {
            var Q0;
            Q0=makeQuery(id+"F6.imprint","IMPRINT",FACE,{"disambiguationData":[TD([[makeQuery(id+"F6.imprint","IMPRINT",EDGE,{"derivedFrom":sQuery(id+"F6.wireOp",EDGE,"E5.bottom")}),-1.0]])]});
            extrude(context, id + "F9", {"entities" : qUnion([Q0]), "operationType" : NewBodyOperationType.REMOVE, "oppositeDirection" : true, "depth" : 25 * mm});
        }
    });
